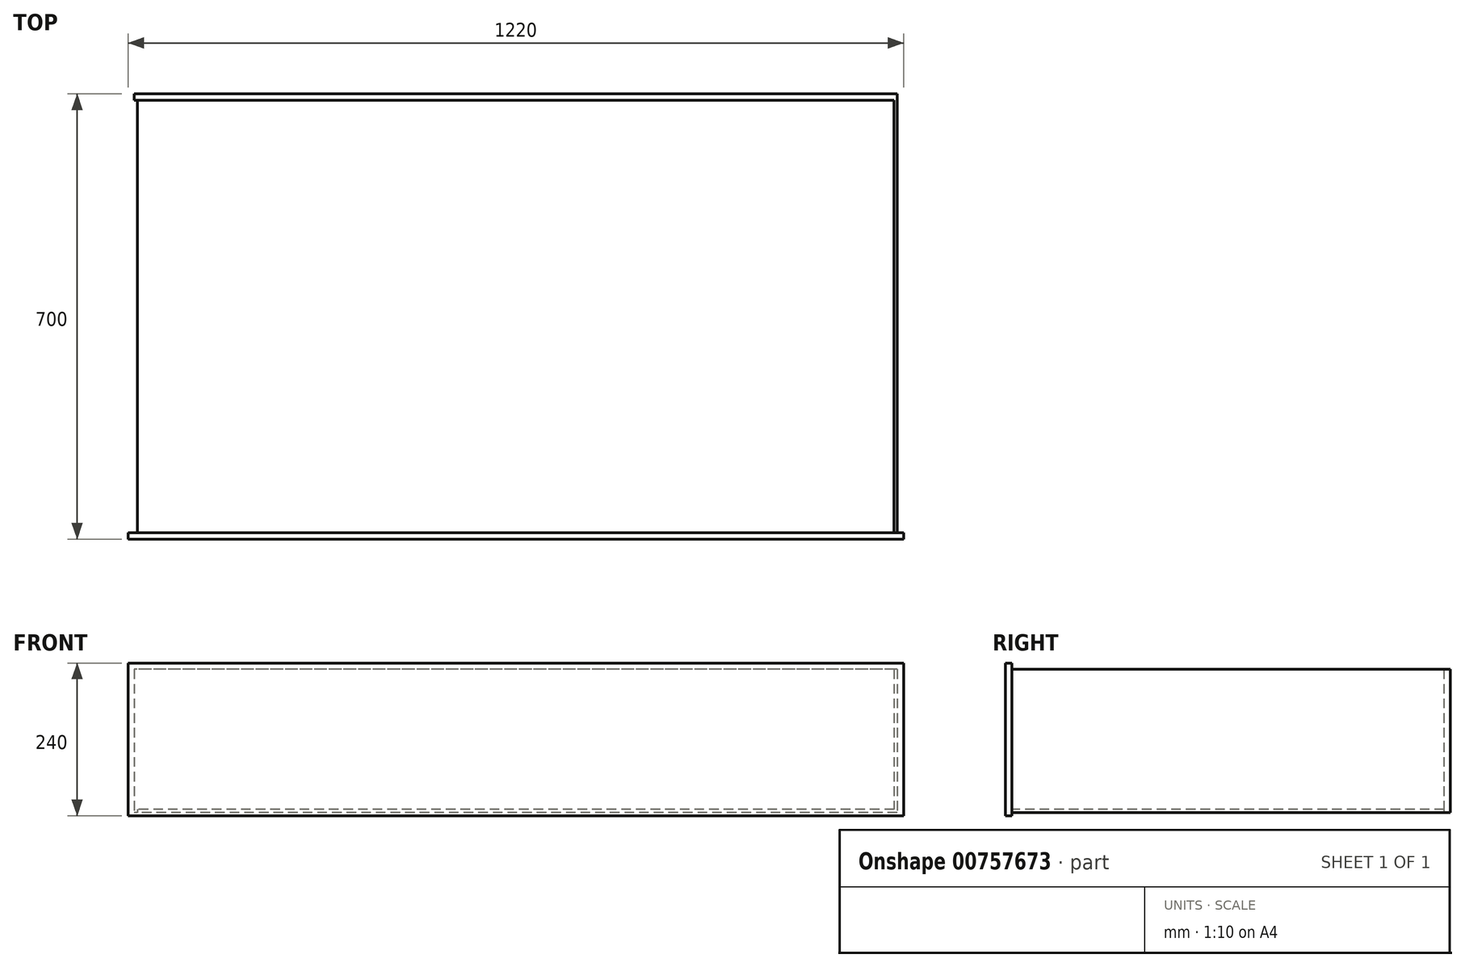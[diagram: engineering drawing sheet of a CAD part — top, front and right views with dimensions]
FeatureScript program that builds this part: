
annotation { "Feature Type Name" : "Feature", "Feature Type Description" : "" }
export const myFeature = defineFeature(function(context is Context, id is Id, definition is map)
    precondition{}
    {
        {
            var Q0;
            Q0=qCreatedBy(makeId("Front.planeOp"),FACE);
            var sketch = newSketch(context, id + "F0", { "sketchPlane" : qUnion([Q0])});
            skLineSegment(sketch, "E0.bottom", {"start": v(-610, 120) * mm, "end": v(610, 120) * mm});
            skLineSegment(sketch, "E0.top", {"start": v(-610, -120) * mm, "end": v(610, -120) * mm});
            skLineSegment(sketch, "E0.left", {"start": v(-610, 120) * mm, "end": v(-610, -120) * mm});
            skLineSegment(sketch, "E0.right", {"start": v(610, 120) * mm, "end": v(610, -120) * mm});
            skSolve(sketch);
        }
        {
            var Q0;
            Q0=makeQuery(id+"F0.imprint","IMPRINT",FACE,{"disambiguationData":[TD([[makeQuery(id+"F0.imprint","IMPRINT",EDGE,{"derivedFrom":sQuery(id+"F0.wireOp",EDGE,"E0.bottom")}),-1.0]])]});
            extrude(context, id + "F1", {"entities" : qUnion([Q0]), "depth" : 10 * mm, "offsetDistance" : 25 * mm});
        }
        {
            var Q0;
            Q0=makeQuery(id+"F1.opExtrude","CAP_FACE",FACE,{"disambiguationData":[OSD([sQuery(id+"F0.wireOp",EDGE,"E0.bottom"),sQuery(id+"F0.wireOp",EDGE,"E0.top"),sQuery(id+"F0.wireOp",EDGE,"E0.left"),sQuery(id+"F0.wireOp",EDGE,"E0.right")])],"isStart":true});
            var sketch = newSketch(context, id + "F2", { "sketchPlane" : qUnion([Q0])});
            skLineSegment(sketch, "E1.bottom", {"start": v(-600, 110) * mm, "end": v(-595, 110) * mm});
            skLineSegment(sketch, "E1.top", {"start": v(-600, -115) * mm, "end": v(-595, -115) * mm});
            skLineSegment(sketch, "E1.left", {"start": v(-600, 110) * mm, "end": v(-600, -115) * mm});
            skLineSegment(sketch, "E1.right", {"start": v(-595, 110) * mm, "end": v(-595, -115) * mm});
            skSolve(sketch);
        }
        {
            var Q0;
            Q0=makeQuery(id+"F2.imprint","IMPRINT",FACE,{"disambiguationData":[TD([[makeQuery(id+"F2.imprint","IMPRINT",EDGE,{"derivedFrom":sQuery(id+"F2.wireOp",EDGE,"E1.bottom")}),-1.0]])]});
            extrude(context, id + "F3", {"entities" : qUnion([Q0]), "operationType" : NewBodyOperationType.ADD, "depth" : 680 * mm, "offsetDistance" : 25 * mm});
        }
        {
            var Q0;
            Q0=makeQuery(id+"F3.opExtrude","CAP_FACE",FACE,{"disambiguationData":[OSD([sQuery(id+"F2.wireOp",EDGE,"E1.bottom"),sQuery(id+"F2.wireOp",EDGE,"E1.top"),sQuery(id+"F2.wireOp",EDGE,"E1.left"),sQuery(id+"F2.wireOp",EDGE,"E1.right")])],"isStart":false});
            var sketch = newSketch(context, id + "F4", { "sketchPlane" : qUnion([Q0])});
            skLineSegment(sketch, "E2.bottom", {"start": v(-600, 110) * mm, "end": v(600, 110) * mm});
            skLineSegment(sketch, "E2.top", {"start": v(-600, -115) * mm, "end": v(600, -115) * mm});
            skLineSegment(sketch, "E2.left", {"start": v(-600, 110) * mm, "end": v(-600, -115) * mm});
            skLineSegment(sketch, "E2.right", {"start": v(600, 110) * mm, "end": v(600, -115) * mm});
            skSolve(sketch);
        }
        {
            var Q0;
            {var subQ2=sQuery(id+"F4.wireOp",EDGE,"E2.right");Q0=makeQuery(id+"F4.imprint","IMPRINT",FACE,{"disambiguationData":[TD([[makeQuery(id+"F4.imprint","IMPRINT",EDGE,{"derivedFrom":subQ2}),-1.0]])]});}
            var Q1;
            {var subQ0=sQuery(id+"F4.wireOp",EDGE,"E2.left");Q1=makeQuery(id+"F4.imprint","IMPRINT",FACE,{"disambiguationData":[TD([[makeQuery(id+"F4.imprint","IMPRINT",EDGE,{"derivedFrom":subQ0}),1.0]])]});}
            extrude(context, id + "F5", {"entities" : qUnion([Q0, Q1]), "operationType" : NewBodyOperationType.ADD, "depth" : 10 * mm, "offsetDistance" : 25 * mm});
        }
        {
            var Q0;
            {var subQ0=sQuery(id+"F2.wireOp",EDGE,"E1.top");Q0=makeQuery(id+"F5.boolean.opBoolean","MERGE",FACE,{"derivedFrom":[makeQuery(id+"F3.opExtrude","SWEPT_FACE",FACE,{"disambiguationData":[OSD([subQ0])]}),makeQuery(id+"FekmwOfsuBOeuhf_1.1.F3.opExtrude","SWEPT_FACE",FACE,{"disambiguationData":[OSD([subQ0])]}),makeQuery(id+"F5.opExtrude","SWEPT_FACE",FACE,{"disambiguationData":[OSD([sQuery(id+"F4.wireOp",EDGE,"E2.top")])]})]});}
            var sketch = newSketch(context, id + "F6", { "sketchPlane" : qUnion([Q0])});
            skLineSegment(sketch, "E3.bottom", {"start": v(-595, 0) * mm, "end": v(595, 0) * mm});
            skLineSegment(sketch, "E3.top", {"start": v(-595, -680) * mm, "end": v(595, -680) * mm});
            skLineSegment(sketch, "E3.left", {"start": v(-595, 0) * mm, "end": v(-595, -680) * mm});
            skLineSegment(sketch, "E3.right", {"start": v(595, 0) * mm, "end": v(595, -680) * mm});
            skSolve(sketch);
        }
        {
            var Q0;
            Q0=makeQuery(id+"F6.imprint","IMPRINT",FACE,{"disambiguationData":[TD([[makeQuery(id+"F6.imprint","IMPRINT",EDGE,{"derivedFrom":sQuery(id+"F6.wireOp",EDGE,"E3.bottom")}),-1.0]])]});
            extrude(context, id + "F7", {"entities" : qUnion([Q0]), "operationType" : NewBodyOperationType.ADD, "oppositeDirection" : true, "depth" : 5 * mm, "offsetDistance" : 25 * mm});
        }
    });
